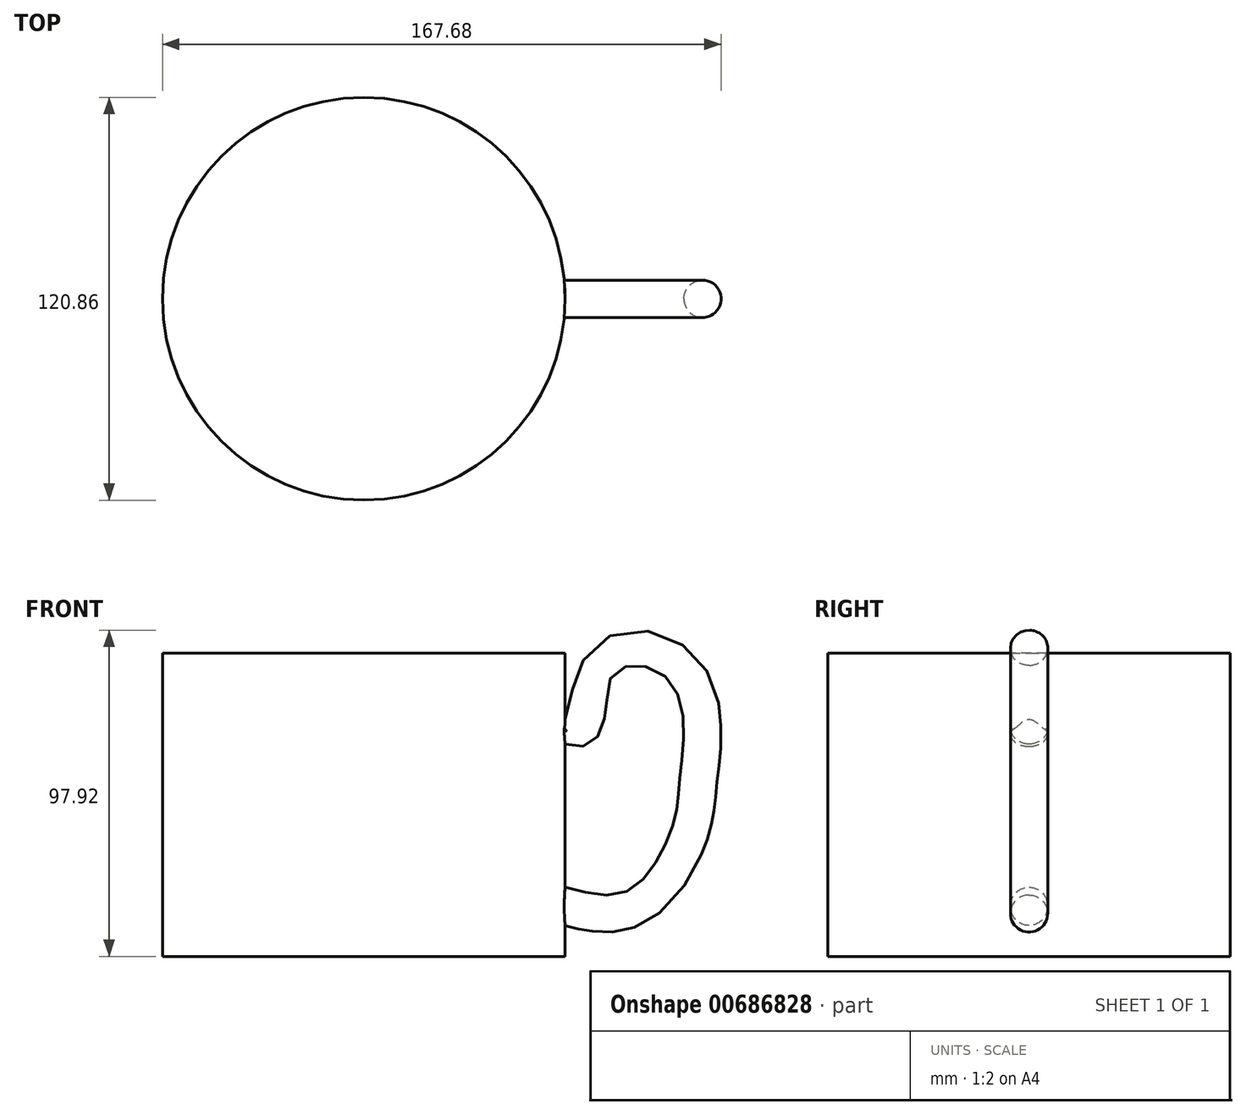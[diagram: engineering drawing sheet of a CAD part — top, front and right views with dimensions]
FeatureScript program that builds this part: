
annotation { "Feature Type Name" : "Feature", "Feature Type Description" : "" }
export const myFeature = defineFeature(function(context is Context, id is Id, definition is map)
    precondition{}
    {
        {
            var Q0;
            Q0=qCreatedBy(makeId("Top.planeOp"),FACE);
            var sketch = newSketch(context, id + "F0", { "sketchPlane" : qUnion([Q0])});
            skCircle(sketch, "E0", {"center": v(0, 0) * mm, "radius": 60.43 * mm});
            skSolve(sketch);
        }
        {
            var Q0;
            Q0=makeQuery(id+"F0.imprint","IMPRINT",FACE,{"disambiguationData":[TD([[makeQuery(id+"F0.imprint","IMPRINT",EDGE,{"derivedFrom":sQuery(id+"F0.wireOp",EDGE,"E0")}),1.0]])]});
            extrude(context, id + "F1", {"entities" : qUnion([Q0]), "depth" : 91 * mm, "offsetDistance" : 25 * mm});
        }
        {
            var Q0;
            Q0=qCreatedBy(makeId("Front.planeOp"),FACE);
            var sketch = newSketch(context, id + "F2", { "sketchPlane" : qUnion([Q0])});
            skFitSpline(sketch, "E1", {"points": [v(51.08, 64.22) * mm, v(70.38, 66.67) * mm, v(78.53, 83.82) * mm, v(91.88, 79.43) * mm, v(93.7, 51.73) * mm, v(90.1, 35.82) * mm, v(75.56, 20.3) * mm, v(49.6, 21.97) * mm], "startDerivative": vector(140.05, 0) * mm, "endDerivative": vector(-156.62, -20.68) * mm});
            skSolve(sketch);
        }
        {
            var Q0;
            Q0=qCreatedBy(makeId("Right.planeOp"),FACE);
            cPlane(context, id + "F3", {"entities" : qUnion([Q0]), "cplaneType" : CPlaneType.OFFSET, "offset" : 45 * mm, "width" : 150 * mm, "height" : 150 * mm});
        }
        {
            var Q0;
            Q0=qCreatedBy(id+"F3.planeOp",FACE);
            var sketch = newSketch(context, id + "F4", { "sketchPlane" : qUnion([Q0])});
            skCircle(sketch, "E2", {"center": v(0, 70.69) * mm, "radius": 5.6 * mm});
            skSolve(sketch);
        }
        {
            var Q0;
            Q0 = qSketchRegion(id + "F4", true);
            var Q1;
            Q1 = qConstructionFilter(qBodyType(qCreatedBy(id + "F2" ,EDGE), BodyType.WIRE), ConstructionObject.NO);
            sweep(context, id + "F5", {"operationType" : NewBodyOperationType.ADD, "profiles" : qUnion([Q0]), "path" : qUnion([Q1])});
        }
    });
